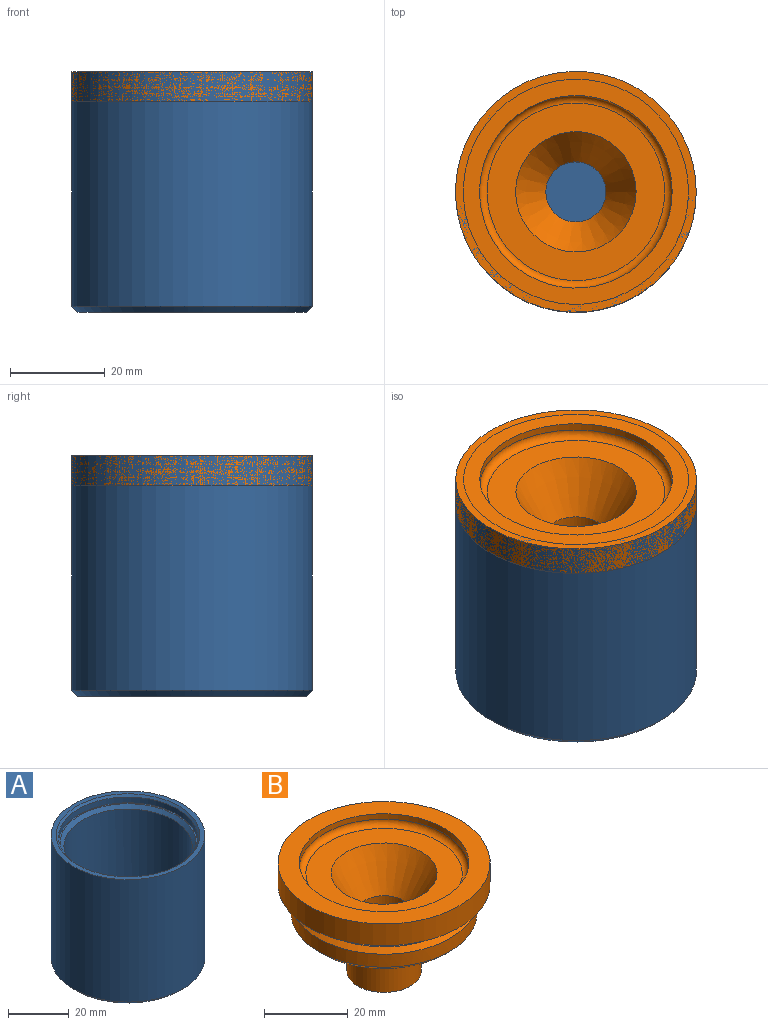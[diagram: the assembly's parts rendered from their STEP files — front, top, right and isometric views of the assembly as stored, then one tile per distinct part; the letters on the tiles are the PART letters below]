
ASSEMBLY  parts=2 mates=1
PART A: 12 faces, bbox 50.8x50.8x50.8 mm
  f0: cylinder r=25.4mm len=50.8mm, axis (0,0,-1), area 7904.6mm2, adj f1,f11
  f1: plane 50.8x50.8mm, normal (0,0,1), area 253mm2, adj f0,f7
  f2: plane 48.26x48.26mm, normal (0,0,-1), area 364.8mm2, adj f10,f11
  f3: cylinder r=23mm len=46mm, axis (0,0,1), area 337.9mm2, adj f4,f7
  f4: plane 46x46mm, normal (0,0,1), area 74.4mm2, adj f3,f8
  f5: cylinder r=21.21mm len=42.42mm, axis (0,0,1), area 5341.1mm2, adj f6,f8
  f6: plane 42.42x42.42mm, normal (0,0,1), area 1413.2mm2, adj f5
  f7: cone r=23mm half-angle=45deg, axis (0,0,1), area 158.3mm2, adj f1,f3
  f8: cone r=21.21mm half-angle=45deg, axis (0,0,1), area 246.5mm2, adj f4,f5
  f9: plane 38.99x38.99mm, normal (0,0,-1), area 1194.2mm2, adj f10
  f10: cone r=21.59mm half-angle=70deg, axis (0,0,-1), area 287.6mm2, adj f2,f9
  f11: cone r=25.4mm half-angle=45deg, axis (0,0,1), area 279.5mm2, adj f0,f2
PART B: 22 faces, bbox 50.8x50.8x31.8 mm
  f0: plane 17.78x17.78mm, normal (0,0,-1), area 121.6mm2, adj f10,f15
  f1: cylinder r=25.4mm len=50.8mm, axis (0,0,1), area 1013.4mm2, adj f2,f3
  f2: plane 50.8x50.8mm, normal (0,0,-1), area 789mm2, adj f1,f7
  f3: plane 50.8x50.8mm, normal (0,0,1), area 729.7mm2, adj f1,f12
  f4: plane 41.91x41.91mm, normal (0,0,-1), area 523.2mm2, adj f8,f14
  f5: cylinder r=22.23mm len=44.45mm, axis (0,0,-1), area 532mm2, adj f8,f9
  f6: plane 41.91x41.91mm, normal (0,0,1), area 141.7mm2, adj f7,f9
  f7: cylinder r=19.85mm len=39.7mm, axis (0,0,-1), area 436.5mm2, adj f2,f6
  f8: cone r=20.96mm half-angle=45deg, axis (0,0,1), area 243.6mm2, adj f4,f5
  f9: cone r=22.23mm half-angle=45deg, axis (0,0,-1), area 243.6mm2, adj f5,f6
  f10: cylinder r=6.35mm len=17.58mm, axis (0,0,1), area 701.3mm2, adj f0,f13
  f11: plane 37.47x37.47mm, normal (0,0,1), area 595.7mm2, adj f13,f21
  f12: cylinder r=20.32mm len=40.64mm, axis (0,0,1), area 202.7mm2, adj f3,f21
  f13: cone r=6.35mm half-angle=30deg, axis (0,0,1), area 760.1mm2, adj f10,f11
  f14: cylinder r=16.51mm len=33.02mm, axis (0,0,1), area 823.4mm2, adj f4,f18
  f15: cylinder r=8.89mm len=17.78mm, axis (0,0,1), area 920mm2, adj f0,f20
  f16: plane 29.85x29.85mm, normal (0,0,-1), area 36.4mm2, adj f18,f19
  f17: cone r=8.89mm half-angle=30deg, axis (0,0,1), area 566.5mm2, adj f19,f20
  f18: torus R=14.92mm, axis (0,0,1), area 249.6mm2, adj f14,f16
  f19: torus R=14.53mm, axis (0,0,1), area 143.8mm2, adj f16,f17
  f20: torus R=10.48mm, axis (0,0,1), area 46.8mm2, adj f15,f17
  f21: torus R=18.73mm, axis (0,0,1), area 309.3mm2, adj f11,f12
PLACE A at identity
PLACE B t=(0,0,50.8)mm
MATE cylindrical B.f1 <-> A.f0  axis (0,0,-1) through (0,0,44.45)mm
